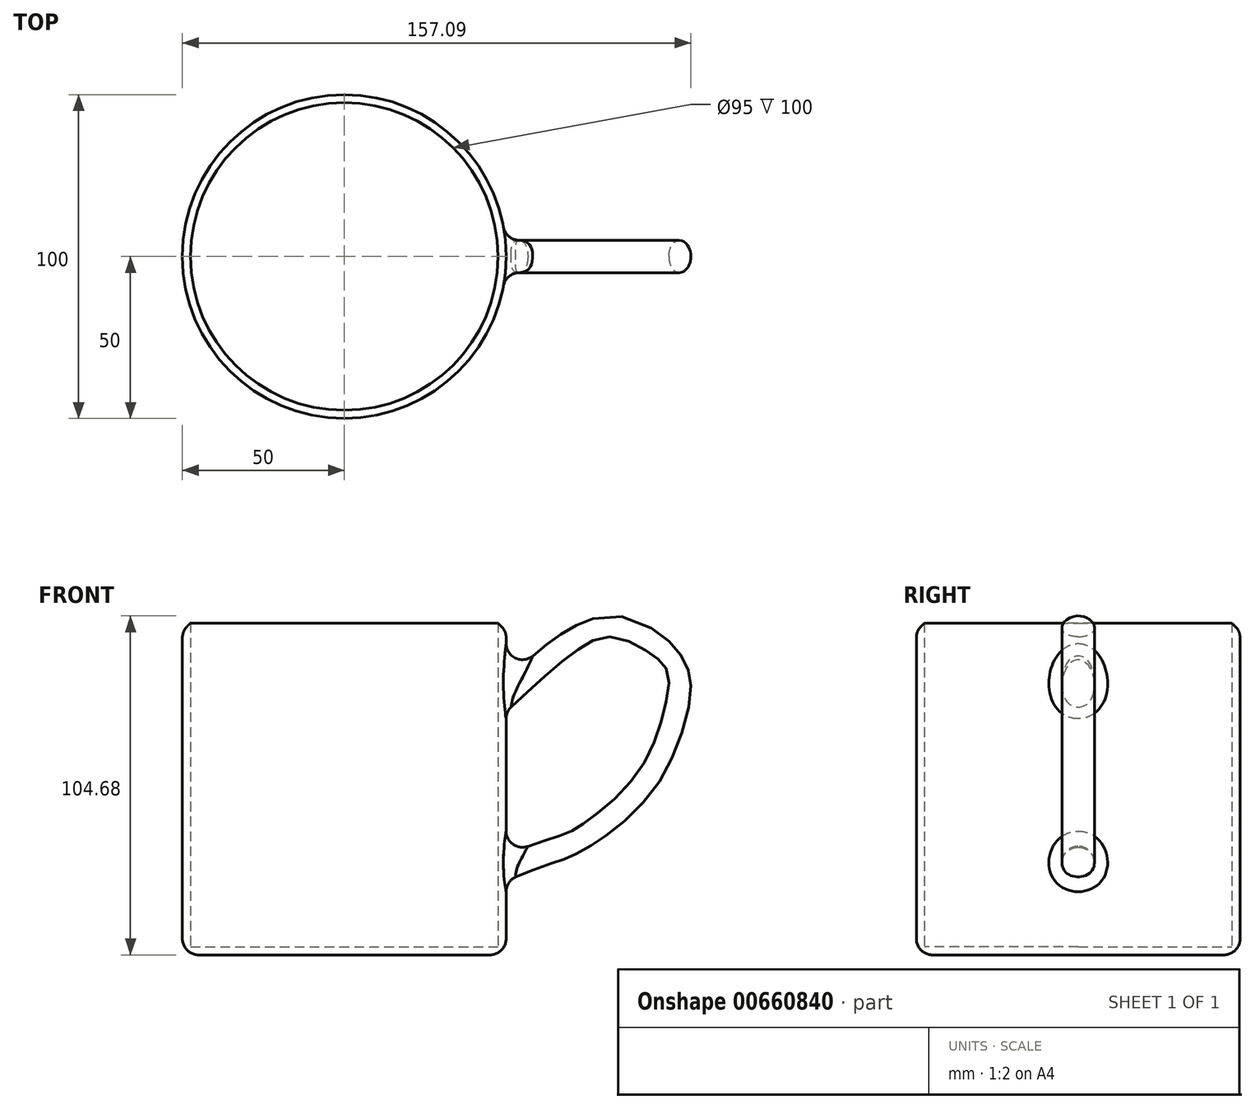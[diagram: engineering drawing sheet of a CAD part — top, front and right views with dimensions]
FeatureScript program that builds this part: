
annotation { "Feature Type Name" : "Feature", "Feature Type Description" : "" }
export const myFeature = defineFeature(function(context is Context, id is Id, definition is map)
    precondition{}
    {
        {
            var Q0;
            Q0=qCreatedBy(makeId("Top.planeOp"),FACE);
            var sketch = newSketch(context, id + "F0", { "sketchPlane" : qUnion([Q0])});
            skCircle(sketch, "E0", {"center": v(0, 0) * mm, "radius": 50 * mm});
            skSolve(sketch);
        }
        {
            var Q0;
            Q0 = qSketchRegion(id + "F0", true);
            extrude(context, id + "F1", {"entities" : qUnion([Q0]), "depth" : 105 * mm, "offsetDistance" : 25 * mm});
        }
        {
            var Q0;
            Q0=qCreatedBy(makeId("Front.planeOp"),FACE);
            var sketch = newSketch(context, id + "F2", { "sketchPlane" : qUnion([Q0])});
            skFitSpline(sketch, "E1", {"points": [v(41.8, 75.1) * mm, v(59.92, 91.74) * mm, v(83.35, 103.06) * mm, v(103.44, 90.43) * mm, v(104.36, 74.74) * mm, v(93.28, 50.6) * mm, v(72.04, 33.15) * mm, v(62.39, 29.33) * mm, v(50.4, 24.58) * mm, v(42.07, 20.06) * mm], "startDerivative": vector(135.06, 130.41) * mm, "endDerivative": vector(-98.05, -57.78) * mm});
            skSolve(sketch);
        }
        {
            var Q0;
            Q0=qCreatedBy(makeId("Right.planeOp"),FACE);
            cPlane(context, id + "F3", {"entities" : qUnion([Q0]), "cplaneType" : CPlaneType.OFFSET, "offset" : 50 * mm, "width" : 150 * mm, "height" : 150 * mm});
        }
        {
            var Q0;
            Q0=qCreatedBy(id+"F3.planeOp",FACE);
            var sketch = newSketch(context, id + "F4", { "sketchPlane" : qUnion([Q0])});
            skCircle(sketch, "E2", {"center": v(0, 80.05) * mm, "radius": 5 * mm});
            skSolve(sketch);
        }
        {
            var Q0;
            Q0=makeQuery(id+"F4.imprint","IMPRINT",FACE,{"disambiguationData":[TD([[makeQuery(id+"F4.imprint","IMPRINT",EDGE,{"derivedFrom":sQuery(id+"F4.wireOp",EDGE,"E2")}),1.0]])]});
            var Q1;
            Q1=sQuery(id+"F2.wireOp",EDGE,"E1");
            sweep(context, id + "F5", {"operationType" : NewBodyOperationType.ADD, "profiles" : qUnion([Q0]), "path" : qUnion([Q1])});
        }
        {
            var Q0;
            Q0=makeQuery(id+"F1.opExtrude","CAP_FACE",FACE,{"disambiguationData":[OSD([sQuery(id+"F0.wireOp",EDGE,"E0")])],"isStart":false});
            shell(context, id + "F6", {"entities" : qUnion([Q0]), "thickness" : 2.5 * mm});
        }
        {
            var Q0;
            Q0=makeQuery(id+"F1.opExtrude","CAP_EDGE",EDGE,{"disambiguationData":[OSD([sQuery(id+"F0.wireOp",EDGE,"E0")])],"isStart":false});
            chamfer(context, id + "F7", {"entities" : qUnion([Q0]), "width" : 5 * mm, "tangentPropagation" : true});
        }
        {
            var Q0;
            Q0=makeQuery(id+"F1.opExtrude","SWEPT_FACE",FACE,{"disambiguationData":[OSD([sQuery(id+"F0.wireOp",EDGE,"E0")])]});
            fillet(context, id + "F8", {"entities" : qUnion([Q0]), "radius" : 5 * mm, "tangentPropagation" : true, "allowEdgeOverflow" : false});
        }
    });
